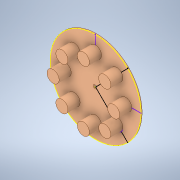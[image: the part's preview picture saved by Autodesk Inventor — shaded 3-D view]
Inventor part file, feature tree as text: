
AUTODESK INVENTOR PART (.ipt)
format: ipt  version: 2021.1 (Build 251245010, 245A)  size: 209,920 bytes
history: native  units: mm
features: sketch x3, extrude x2, other x1, pattern_circular x1
ambient origin geometry x8: Origin, YZ Plane, XZ Plane, XY Plane, X Axis, Y Axis, Z Axis, Center Point
bodies: Solid2 (feature_tree), Solid1 (feature_tree)
feature tree (7):
  other  "Repaired Geometry1"
  extrude  "Extrusion1"  Depth=4.0mm
  sketch  "Sketch2"  dims[d3=40.0mm d4=40.0mm d5=0.0mm d6=80.0mm d7=62.831853mm]
  extrude  "Extrusion2"  Depth=40.0mm TaperAngle=0.0deg
  pattern_circular  "Circular Pattern1"  Count=8  [1 undecoded]
  sketch  "Sketch3"
  sketch  "Sketch1"  dims[d0=4.0mm d1=0.0mm d2=100.0mm]
note: 1 required parameter value undecoded (feature->parameter linkage not recoverable at this tier; creation-order binding heuristic only, values carry confidence <= 0.55)
